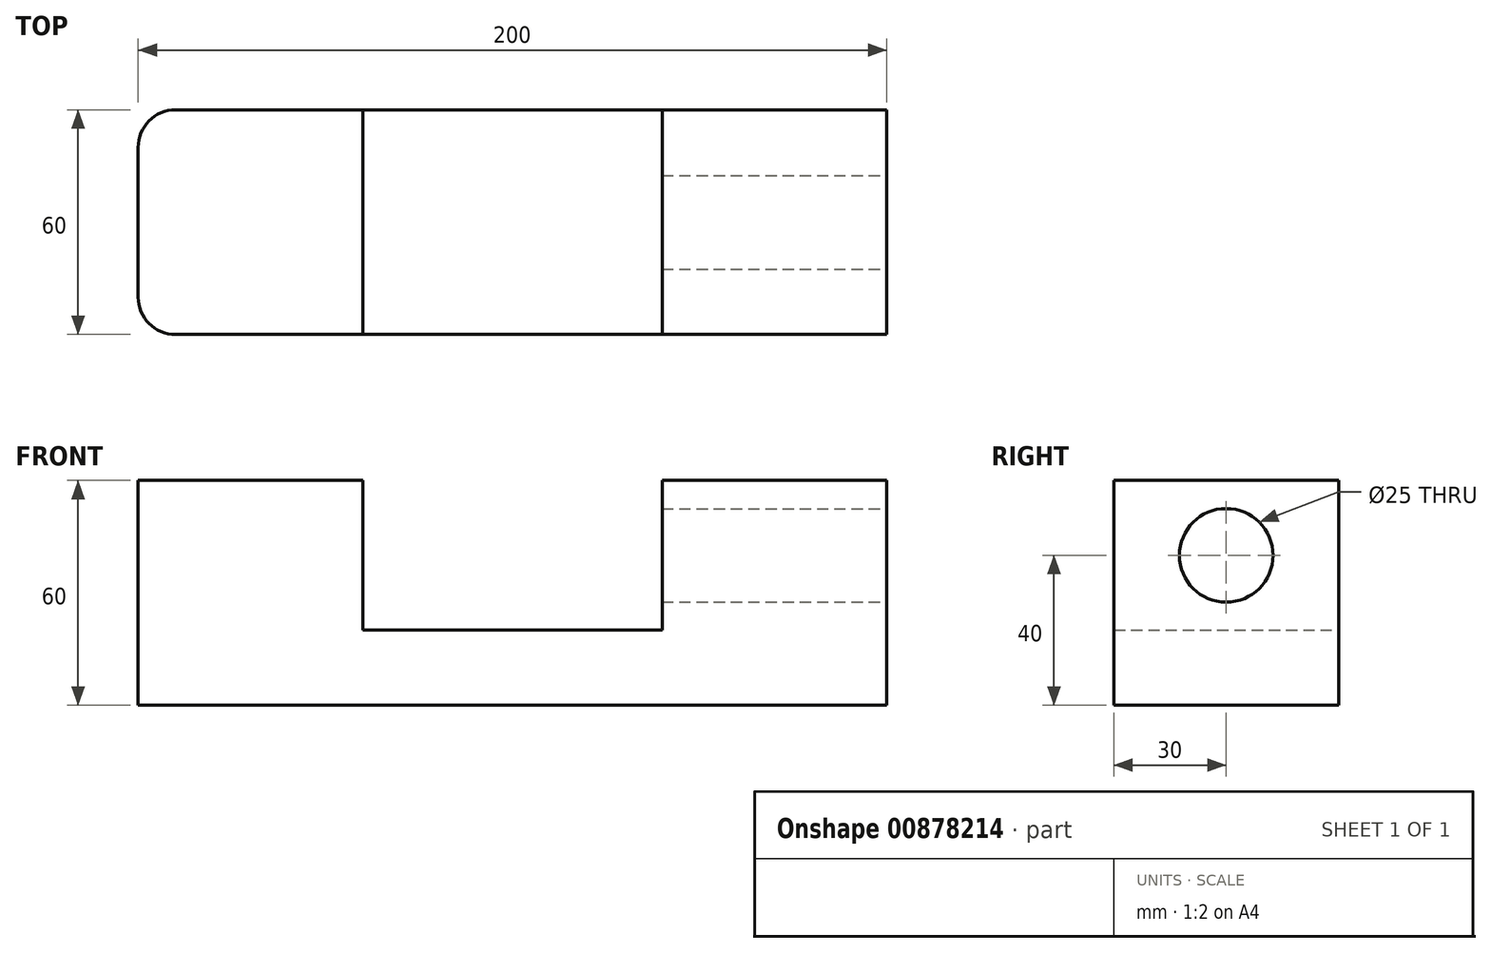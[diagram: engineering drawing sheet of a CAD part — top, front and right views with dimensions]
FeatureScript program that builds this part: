
annotation { "Feature Type Name" : "Feature", "Feature Type Description" : "" }
export const myFeature = defineFeature(function(context is Context, id is Id, definition is map)
    precondition{}
    {
        {
            var Q0;
            Q0=qCreatedBy(makeId("Front.planeOp"),FACE);
            var sketch = newSketch(context, id + "F0", { "sketchPlane" : qUnion([Q0])});
            skLineSegment(sketch, "E0.bottom", {"start": v(0, 0) * mm, "end": v(200, 0) * mm});
            skLineSegment(sketch, "E0.left", {"start": v(0, 0) * mm, "end": v(0, 60) * mm});
            skLineSegment(sketch, "E0.right", {"start": v(200, 0) * mm, "end": v(200, 60) * mm});
            skLineSegment(sketch, "E1", {"start": v(200, 60) * mm, "end": v(140, 60) * mm});
            skLineSegment(sketch, "E2", {"start": v(140, 60) * mm, "end": v(140, 20) * mm});
            skLineSegment(sketch, "E3", {"start": v(140, 20) * mm, "end": v(60, 20) * mm});
            skLineSegment(sketch, "E4", {"start": v(60, 20) * mm, "end": v(60, 60) * mm});
            skLineSegment(sketch, "E5", {"start": v(60, 60) * mm, "end": v(0, 60) * mm});
            skSolve(sketch);
        }
        {
            var Q0;
            Q0=makeQuery(id+"F0.imprint","IMPRINT",FACE,{"disambiguationData":[TD([[makeQuery(id+"F0.imprint","IMPRINT",EDGE,{"derivedFrom":sQuery(id+"F0.wireOp",EDGE,"E0.bottom")}),1.0]])]});
            extrude(context, id + "F1", {"entities" : qUnion([Q0]), "depth" : 60 * mm, "offsetDistance" : 25 * mm});
        }
        {
            var Q0;
            Q0=makeQuery(id+"F1.opExtrude","SWEPT_FACE",FACE,{"disambiguationData":[OSD([sQuery(id+"F0.wireOp",EDGE,"E0.right")])]});
            var sketch = newSketch(context, id + "F2", { "sketchPlane" : qUnion([Q0])});
            skCircle(sketch, "E6", {"center": v(-30, 40) * mm, "radius": 12.5 * mm});
            skLineSegment(sketch, "E7", {"start": v(-30, 60) * mm, "end": v(-30, 0) * mm});
            skLineSegment(sketch, "E8", {"start": v(-30, 40) * mm, "end": v(0, 40) * mm});
            skLineSegment(sketch, "E9", {"start": v(0, 40) * mm, "end": v(-60, 40) * mm});
            skLineSegment(sketch, "E10", {"start": v(-30, 40) * mm, "end": v(-30, 0) * mm});
            skSolve(sketch);
        }
        {
            var Q0;
            Q0=makeQuery(id+"F2.imprint","IMPRINT",FACE,{"disambiguationData":[TD([[makeQuery(id+"F2.imprint","IMPRINT",EDGE,{"derivedFrom":sQuery(id+"F2.wireOp",EDGE,"E6")}),1.0]])]});
            extrude(context, id + "F3", {"entities" : qUnion([Q0]), "operationType" : NewBodyOperationType.REMOVE, "oppositeDirection" : true, "depth" : 60 * mm, "offsetDistance" : 25 * mm});
        }
        {
            var Q0;
            Q0=makeQuery(id+"F1.opExtrude","CAP_EDGE",EDGE,{"disambiguationData":[OSD([sQuery(id+"F0.wireOp",EDGE,"E0.left")])],"isStart":true});
            var Q1;
            Q1=makeQuery(id+"F1.opExtrude","CAP_EDGE",EDGE,{"disambiguationData":[OSD([sQuery(id+"F0.wireOp",EDGE,"E0.left")])],"isStart":false});
            fillet(context, id + "F4", {"entities" : qUnion([Q0, Q1]), "radius" : 10 * mm, "tangentPropagation" : true, "allowEdgeOverflow" : false});
        }
    });
